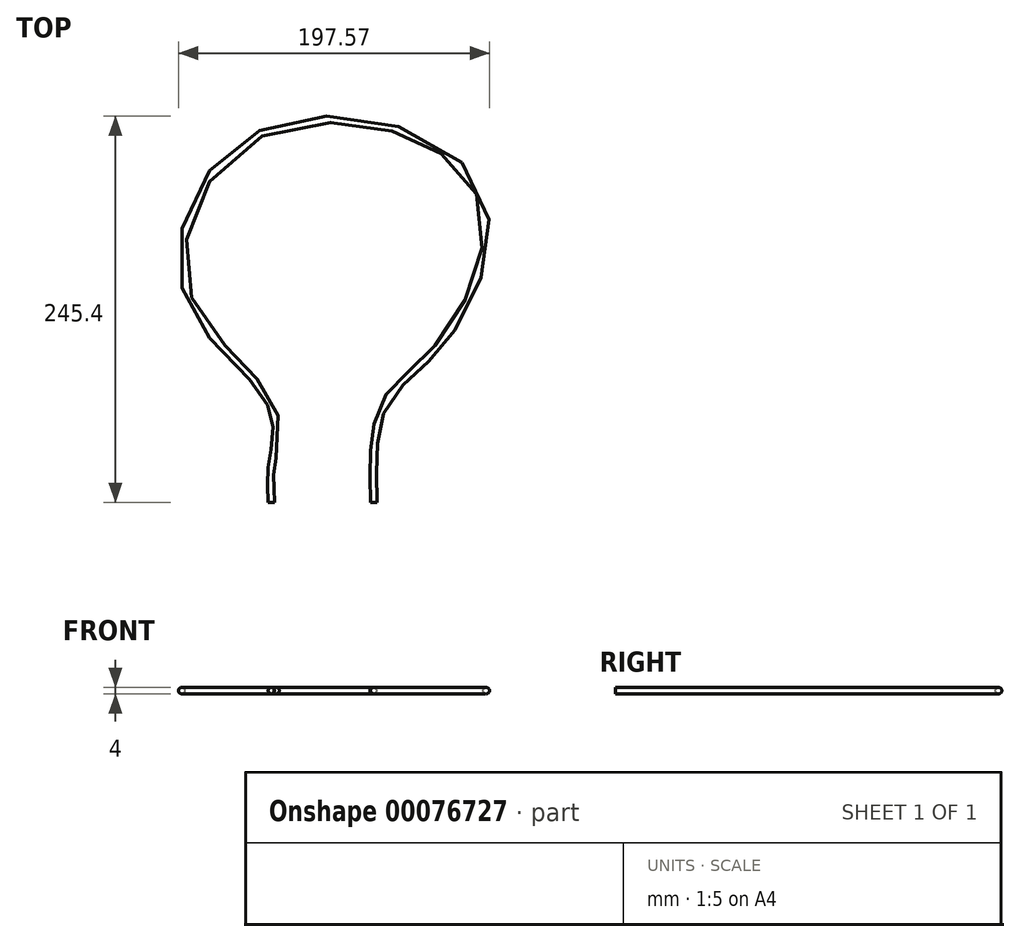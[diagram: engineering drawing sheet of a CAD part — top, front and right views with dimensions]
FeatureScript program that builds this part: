
annotation { "Feature Type Name" : "Feature", "Feature Type Description" : "" }
export const myFeature = defineFeature(function(context is Context, id is Id, definition is map)
    precondition{}
    {
        {
            var Q0;
            Q0=qCreatedBy(makeId("Top.planeOp"),FACE);
            var sketch = newSketch(context, id + "F0", { "sketchPlane" : qUnion([Q0])});
            skFitSpline(sketch, "E0", {"points": [v(0, 0) * mm, v(0, 22.35) * mm, v(0, 61.72) * mm, v(-53.52, 132.01) * mm, v(-7.76, 234) * mm, v(128.6, 203.46) * mm, v(111.54, 105.6) * mm, v(74.76, 67.78) * mm, v(65.74, 41.18) * mm, v(65.02, 0) * mm], "startDerivative": vector(-11.37, 531.52) * mm, "endDerivative": vector(13.87, -634.9) * mm});
            skSolve(sketch);
        }
        {
            var Q0;
            Q0=qCreatedBy(makeId("Front.planeOp"),FACE);
            var sketch = newSketch(context, id + "F1", { "sketchPlane" : qUnion([Q0])});
            skCircle(sketch, "E1", {"center": v(0, 0) * mm, "radius": 2 * mm});
            skSolve(sketch);
        }
        {
            var Q0;
            Q0 = qSketchRegion(id + "F1", true);
            var Q1;
            Q1 = qConstructionFilter(qBodyType(qCreatedBy(id + "F0" ,EDGE), BodyType.WIRE), ConstructionObject.NO);
            sweep(context, id + "F2", {"profiles" : qUnion([Q0]), "path" : qUnion([Q1])});
        }
    });
